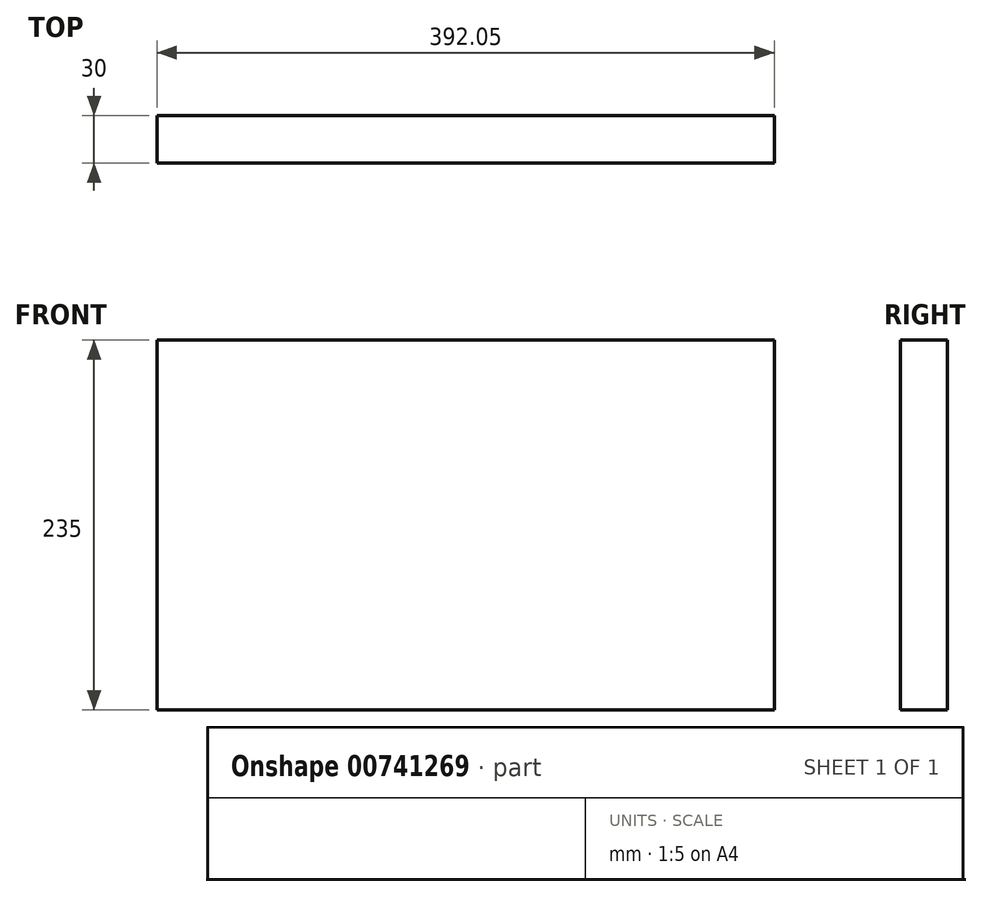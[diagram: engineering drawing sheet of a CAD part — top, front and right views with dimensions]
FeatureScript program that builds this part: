
annotation { "Feature Type Name" : "Feature", "Feature Type Description" : "" }
export const myFeature = defineFeature(function(context is Context, id is Id, definition is map)
    precondition{}
    {
        {
            var Q0;
            Q0=qCreatedBy(makeId("Front.planeOp"),FACE);
            var sketch = newSketch(context, id + "F0", { "sketchPlane" : qUnion([Q0])});
            skLineSegment(sketch, "E0.bottom", {"start": v(-171.57, 110.9) * mm, "end": v(220.48, 110.9) * mm});
            skLineSegment(sketch, "E0.top", {"start": v(-171.57, -124.1) * mm, "end": v(220.48, -124.1) * mm});
            skLineSegment(sketch, "E0.left", {"start": v(-171.57, 110.9) * mm, "end": v(-171.57, -124.1) * mm});
            skLineSegment(sketch, "E0.right", {"start": v(220.48, 110.9) * mm, "end": v(220.48, -124.1) * mm});
            skSolve(sketch);
        }
        {
            var Q0;
            Q0=makeQuery(id+"F0.imprint","IMPRINT",FACE,{"disambiguationData":[TD([[makeQuery(id+"F0.imprint","IMPRINT",EDGE,{"derivedFrom":sQuery(id+"F0.wireOp",EDGE,"E0.bottom")}),-1.0]])]});
            extrude(context, id + "F1", {"entities" : qUnion([Q0]), "depth" : 30 * mm, "offsetDistance" : 25 * mm});
        }
    });
